# Revit family: ACORN_Flood_VIZULO
name_source: partatom
category: Lighting Fixtures
units: mm (PartAtom-declared; Revit-internal decimal feet)

## family parameters
Always vertical = Yes
Cut with Voids When Loaded = No
Light Source = Yes
OmniClass Number = 23.80.70.00
OmniClass Title = Lighting
Part Type = Normal
Room Calculation Point = No
Round Connector Dimension = Use Diameter
Shared = No
Work Plane-Based = No

## types (738) — shared parameters
Color Filter = 16777215
Dimming Lamp Color Temperature Shift = <None>
Emit Shape Visible in Rendering = No
Emit from Circle Diameter = 300 mm
Light Source Symbol Length = 3048 mm  [stored 10 ft]
Tilt Angle = 90.00°

## per-type parameters (varying)
| type | Default Elevation | Spot Beam Angle | Spot Field Angle |
| CO1, 20 W, 3000 K, 90° | 0 mm  [stored 0 ft] | 50.00° | 30.00° |
| CO1, 20 W, 4000 K, 90° | 0 mm  [stored 0 ft] | 30.00° | 50.00° |
| CO1, 270 W, 3000 K. 0° | 0 mm  [stored 0 ft] | 50.00° | 30.00° |
| CO1, 270 W, 4000 K, 0° | 0 mm  [stored 0 ft] | 50.00° | 30.00° |
| CO2, 20 W, 3000 K, 0° | 0 mm  [stored 0 ft] | 50.00° | 30.00° |
| CO2, 270 W, 4000 K, 0° | 0 mm  [stored 0 ft] | 50.00° | 30.00° |
| CO2, 20 W, 4000 K, 0° | 0 mm  [stored 0 ft] | 50.00° | 30.00° |
| CO2, 270 W, 3000 K, 0° | 0 mm  [stored 0 ft] | 50.00° | 30.00° |
| DO2, 20 W, 3000 K, 0° | 0 mm  [stored 0 ft] | 30.00° | 30.00° |
| DO2, 20 W, 4000 K, 0° | 0 mm  [stored 0 ft] | 30.00° | 30.00° |
| DO2, 270 W, 3000 K, 0° | 0 mm  [stored 0 ft] | 30.00° | 30.00° |
| DO2, 270 W, 4000 K, 0° | 0 mm  [stored 0 ft] | 30.00° | 30.00° |
| DO3, 20 W, 3000 K, 0° | 0 mm  [stored 0 ft] | 45.00° | 45.00° |
| DO3, 20 W, 4000 K, 0° | 0 mm  [stored 0 ft] | 45.00° | 45.00° |
| DO3, 270 W, 3000 K, 0° | 0 mm  [stored 0 ft] | 45.00° | 45.00° |
| DO3, 270 W, 4000 K, 0° | 0 mm  [stored 0 ft] | 45.00° | 45.00° |
| CO3, 20 W, 3000 K, 0° | 0 mm  [stored 0 ft] | 65.00° | 45.00° |
| CO3, 20 W, 4000 K, 0° | 0 mm  [stored 0 ft] | 65.00° | 45.00° |
| CO3, 270 W, 3000 K, 0° | 0 mm  [stored 0 ft] | 65.00° | 45.00° |
| CO3, 270 W, 4000 K, 0° | 0 mm  [stored 0 ft] | 65.00° | 45.00° |
| CO1, 20 W, 3000 K, 0° | 0 mm  [stored 0 ft] | 50.00° | 30.00° |
| CO1, 20 W, 3000 K, 180° | 0 mm  [stored 0 ft] | 50.00° | 30.00° |
| CO1, 20 W, 4000 K, 0° | 0 mm  [stored 0 ft] | 30.00° | 50.00° |
| CO1, 20 W, 4000 K, 180° | 0 mm  [stored 0 ft] | 30.00° | 50.00° |
| CO1, 270 W, 3000 K. 90° | 0 mm  [stored 0 ft] | 50.00° | 30.00° |
| CO1, 270 W, 3000 K. 180° | 0 mm  [stored 0 ft] | 50.00° | 30.00° |
| CO1, 270 W, 4000 K, 90° | 0 mm  [stored 0 ft] | 50.00° | 30.00° |
| CO1, 270 W, 4000 K, 180° | 0 mm  [stored 0 ft] | 50.00° | 30.00° |
| CO2, 20 W, 3000 K, 90° | 0 mm  [stored 0 ft] | 50.00° | 30.00° |
| CO2, 20 W, 3000 K, 180° | 0 mm  [stored 0 ft] | 50.00° | 30.00° |
| CO2, 20 W, 4000 K, 90° | 0 mm  [stored 0 ft] | 50.00° | 30.00° |
| CO2, 20 W, 4000 K, 180° | 0 mm  [stored 0 ft] | 50.00° | 30.00° |
| CO2, 270 W, 3000 K, 90° | 0 mm  [stored 0 ft] | 50.00° | 30.00° |
| CO2, 270 W, 3000 K, 180° | 0 mm  [stored 0 ft] | 50.00° | 30.00° |
| CO2, 270 W, 4000 K, 90° | 0 mm  [stored 0 ft] | 50.00° | 30.00° |
| CO2, 270 W, 4000 K, 180° | 0 mm  [stored 0 ft] | 50.00° | 30.00° |
| CO3, 20 W, 3000 K, 90° | 0 mm  [stored 0 ft] | 65.00° | 45.00° |
| CO3, 20 W, 3000 K, 180° | 0 mm  [stored 0 ft] | 65.00° | 45.00° |
| CO3, 20 W, 4000 K, 90° | 0 mm  [stored 0 ft] | 65.00° | 45.00° |
| CO3, 20 W, 4000 K, 180° | 0 mm  [stored 0 ft] | 65.00° | 45.00° |
| CO3, 270 W, 3000 K, 90° | 0 mm  [stored 0 ft] | 65.00° | 45.00° |
| CO3, 270 W, 3000 K, 180° | 0 mm  [stored 0 ft] | 65.00° | 45.00° |
| CO3, 270 W, 4000 K, 90° | 0 mm  [stored 0 ft] | 65.00° | 45.00° |
| CO3, 270 W, 4000 K, 180° | 0 mm  [stored 0 ft] | 65.00° | 45.00° |
| DO2, 20 W, 3000 K, 90° | 0 mm  [stored 0 ft] | 30.00° | 30.00° |
| DO2, 20 W, 3000 K, 180° | 0 mm  [stored 0 ft] | 30.00° | 30.00° |
| DO2, 20 W, 4000 K, 90° | 0 mm  [stored 0 ft] | 30.00° | 30.00° |
| DO2, 20 W, 4000 K, 180° | 0 mm  [stored 0 ft] | 30.00° | 30.00° |
| DO2, 270 W, 3000 K, 90° | 0 mm  [stored 0 ft] | 30.00° | 30.00° |
| DO2, 270 W, 3000 K, 180° | 0 mm  [stored 0 ft] | 30.00° | 30.00° |
| DO2, 270 W, 4000 K, 90° | 0 mm  [stored 0 ft] | 30.00° | 30.00° |
| DO2, 270 W, 4000 K, 180° | 0 mm  [stored 0 ft] | 30.00° | 30.00° |
| DO3, 20 W, 3000 K, 90° | 0 mm  [stored 0 ft] | 45.00° | 45.00° |
| DO3, 20 W, 3000 K, 180° | 0 mm  [stored 0 ft] | 45.00° | 45.00° |
| DO3, 20 W, 4000 K, 90° | 0 mm  [stored 0 ft] | 45.00° | 45.00° |
| DO3, 20 W, 4000 K, 180° | 0 mm  [stored 0 ft] | 45.00° | 45.00° |
| DO3, 270 W, 3000 K, 90° | 0 mm  [stored 0 ft] | 45.00° | 45.00° |
| DO3, 270 W, 3000 K, 180° | 0 mm  [stored 0 ft] | 45.00° | 45.00° |
| DO3, 270 W, 4000 K, 90° | 0 mm  [stored 0 ft] | 45.00° | 45.00° |
| DO3, 270 W, 4000 K, 180° | 0 mm  [stored 0 ft] | 45.00° | 45.00° |
| CO1, 20 W, 3000 K, 5° | 0 mm  [stored 0 ft] | 50.00° | 30.00° |
| CO1, 20 W, 3000 K, 10° | 0 mm  [stored 0 ft] | 50.00° | 30.00° |
| CO1, 20 W, 3000 K, 15° | 0 mm  [stored 0 ft] | 50.00° | 30.00° |
| CO1, 20 W, 3000 K, 20° | 0 mm  [stored 0 ft] | 50.00° | 30.00° |
| CO1, 20 W, 3000 K, 25° | 0 mm  [stored 0 ft] | 50.00° | 30.00° |
| CO1, 20 W, 3000 K, 30° | 0 mm  [stored 0 ft] | 50.00° | 30.00° |
| CO1, 20 W, 3000 K, 35° | 0 mm  [stored 0 ft] | 50.00° | 30.00° |
| CO1, 20 W, 3000 K, 40° | 0 mm  [stored 0 ft] | 50.00° | 30.00° |
| CO1, 20 W, 3000 K, 45° | 0 mm  [stored 0 ft] | 50.00° | 30.00° |
| CO1, 20 W, 3000 K, 50° | 0 mm  [stored 0 ft] | 50.00° | 30.00° |
| CO1, 20 W, 3000 K, 55° | 0 mm  [stored 0 ft] | 50.00° | 30.00° |
| CO1, 20 W, 3000 K, 60° | 0 mm  [stored 0 ft] | 50.00° | 30.00° |
| CO1, 20 W, 3000 K, 65° | 0 mm  [stored 0 ft] | 50.00° | 30.00° |
| CO1, 20 W, 3000 K, 70° | 0 mm  [stored 0 ft] | 50.00° | 30.00° |
| CO1, 20 W, 3000 K, 75° | 0 mm  [stored 0 ft] | 50.00° | 30.00° |
| CO1, 20 W, 3000 K, 80° | 0 mm  [stored 0 ft] | 50.00° | 30.00° |
| CO1, 20 W, 3000 K, 85° | 0 mm  [stored 0 ft] | 50.00° | 30.00° |
| CO1, 20 W, 3000 K, 95° | 0 mm  [stored 0 ft] | 50.00° | 30.00° |
| CO1, 20 W, 3000 K, 100° | 0 mm  [stored 0 ft] | 50.00° | 30.00° |
| CO1, 20 W, 3000 K, 105° | 0 mm  [stored 0 ft] | 50.00° | 30.00° |
| CO1, 20 W, 3000 K, 110° | 0 mm  [stored 0 ft] | 50.00° | 30.00° |
| CO1, 20 W, 3000 K, 115° | 0 mm  [stored 0 ft] | 50.00° | 30.00° |
| CO1, 20 W, 3000 K, 120° | 0 mm  [stored 0 ft] | 50.00° | 30.00° |
| CO1, 20 W, 3000 K, 125° | 0 mm  [stored 0 ft] | 50.00° | 30.00° |
| CO1, 20 W, 3000 K, 130° | 0 mm  [stored 0 ft] | 50.00° | 30.00° |
| CO1, 20 W, 3000 K, 135° | 0 mm  [stored 0 ft] | 50.00° | 30.00° |
| CO1, 20 W, 3000 K, 140° | 0 mm  [stored 0 ft] | 50.00° | 30.00° |
| CO1, 20 W, 3000 K, 145° | 0 mm  [stored 0 ft] | 50.00° | 30.00° |
| CO1, 20 W, 3000 K, 150° | 0 mm  [stored 0 ft] | 50.00° | 30.00° |
| CO1, 20 W, 3000 K, 165° | 0 mm  [stored 0 ft] | 50.00° | 30.00° |
| CO1, 20 W, 3000 K, 170° | 0 mm  [stored 0 ft] | 50.00° | 30.00° |
| CO1, 20 W, 3000 K, 175° | 0 mm  [stored 0 ft] | 50.00° | 30.00° |
| CO1, 20 W, 4000 K, 5° | 0 mm  [stored 0 ft] | 30.00° | 50.00° |
| CO1, 20 W, 4000 K, 10° | 0 mm  [stored 0 ft] | 30.00° | 50.00° |
| CO1, 20 W, 4000 K, 15° | 0 mm  [stored 0 ft] | 30.00° | 50.00° |
| CO1, 20 W, 4000 K, 20° | 0 mm  [stored 0 ft] | 30.00° | 50.00° |
| CO1, 20 W, 4000 K, 25° | 0 mm  [stored 0 ft] | 30.00° | 50.00° |
| CO1, 20 W, 4000 K, 30° | 0 mm  [stored 0 ft] | 30.00° | 50.00° |
| CO1, 20 W, 4000 K, 35° | 0 mm  [stored 0 ft] | 30.00° | 50.00° |
| CO1, 20 W, 4000 K, 40° | 0 mm  [stored 0 ft] | 30.00° | 50.00° |
| CO1, 20 W, 4000 K, 45° | 0 mm  [stored 0 ft] | 30.00° | 50.00° |
| CO1, 20 W, 4000 K, 50° | 0 mm  [stored 0 ft] | 30.00° | 50.00° |
| CO1, 20 W, 4000 K, 55° | 0 mm  [stored 0 ft] | 30.00° | 50.00° |
| CO1, 20 W, 4000 K, 60° | 0 mm  [stored 0 ft] | 30.00° | 50.00° |
| CO1, 20 W, 4000 K, 65° | 0 mm  [stored 0 ft] | 30.00° | 50.00° |
| CO1, 20 W, 4000 K, 70° | 0 mm  [stored 0 ft] | 30.00° | 50.00° |
| CO1, 20 W, 4000 K, 75° | 0 mm  [stored 0 ft] | 30.00° | 50.00° |
| CO1, 20 W, 4000 K, 80° | 0 mm  [stored 0 ft] | 30.00° | 50.00° |
| CO1, 20 W, 4000 K, 85° | 0 mm  [stored 0 ft] | 30.00° | 50.00° |
| CO1, 20 W, 4000 K, 95° | 0 mm  [stored 0 ft] | 30.00° | 50.00° |
| CO1, 20 W, 4000 K, 100° | 0 mm  [stored 0 ft] | 30.00° | 50.00° |
| CO1, 20 W, 4000 K, 105° | 0 mm  [stored 0 ft] | 30.00° | 50.00° |
| CO1, 20 W, 4000 K, 110° | 0 mm  [stored 0 ft] | 30.00° | 50.00° |
| CO1, 20 W, 4000 K, 115° | 0 mm  [stored 0 ft] | 30.00° | 50.00° |
| CO1, 20 W, 4000 K, 120° | 0 mm  [stored 0 ft] | 30.00° | 50.00° |
| CO1, 20 W, 4000 K, 125° | 0 mm  [stored 0 ft] | 30.00° | 50.00° |
| CO1, 20 W, 4000 K, 130° | 0 mm  [stored 0 ft] | 30.00° | 50.00° |
| CO1, 20 W, 4000 K, 135° | 0 mm  [stored 0 ft] | 30.00° | 50.00° |
| CO1, 20 W, 4000 K, 140° | 0 mm  [stored 0 ft] | 30.00° | 50.00° |
| CO1, 20 W, 4000 K, 145° | 0 mm  [stored 0 ft] | 30.00° | 50.00° |
| CO1, 20 W, 4000 K, 150° | 0 mm  [stored 0 ft] | 30.00° | 50.00° |
| CO1, 20 W, 4000 K, 155° | 0 mm  [stored 0 ft] | 30.00° | 50.00° |
| CO1, 20 W, 4000 K, 160° | 0 mm  [stored 0 ft] | 30.00° | 50.00° |
| CO1, 20 W, 4000 K, 165° | 0 mm  [stored 0 ft] | 30.00° | 50.00° |
| CO1, 20 W, 4000 K, 170° | 0 mm  [stored 0 ft] | 30.00° | 50.00° |
| CO1, 20 W, 4000 K, 175° | 0 mm  [stored 0 ft] | 30.00° | 50.00° |
| CO1, 270 W, 3000 K. 5° | 0 mm  [stored 0 ft] | 50.00° | 30.00° |
| CO1, 270 W, 3000 K. 10° | 0 mm  [stored 0 ft] | 50.00° | 30.00° |
| CO1, 270 W, 3000 K. 15° | 0 mm  [stored 0 ft] | 50.00° | 30.00° |
| CO1, 270 W, 3000 K. 20° | 0 mm  [stored 0 ft] | 50.00° | 30.00° |
| CO1, 270 W, 3000 K. 25° | 0 mm  [stored 0 ft] | 50.00° | 30.00° |
| CO1, 270 W, 3000 K. 30° | 0 mm  [stored 0 ft] | 50.00° | 30.00° |
| CO1, 270 W, 3000 K. 35° | 0 mm  [stored 0 ft] | 50.00° | 30.00° |
| CO1, 270 W, 3000 K. 40° | 0 mm  [stored 0 ft] | 50.00° | 30.00° |
| CO1, 270 W, 3000 K. 45° | 0 mm  [stored 0 ft] | 50.00° | 30.00° |
| CO1, 270 W, 3000 K. 50° | 0 mm  [stored 0 ft] | 50.00° | 30.00° |
| CO1, 270 W, 3000 K. 55° | 0 mm  [stored 0 ft] | 50.00° | 30.00° |
| CO1, 270 W, 3000 K. 60° | 0 mm  [stored 0 ft] | 50.00° | 30.00° |
| CO1, 270 W, 3000 K. 65° | 0 mm  [stored 0 ft] | 50.00° | 30.00° |
| CO1, 270 W, 3000 K. 70° | 0 mm  [stored 0 ft] | 50.00° | 30.00° |
| CO1, 270 W, 3000 K. 75° | 0 mm  [stored 0 ft] | 50.00° | 30.00° |
| CO1, 270 W, 3000 K. 80° | 0 mm  [stored 0 ft] | 50.00° | 30.00° |
| CO1, 270 W, 3000 K. 85° | 0 mm  [stored 0 ft] | 50.00° | 30.00° |
| CO1, 270 W, 3000 K. 95° | 0 mm  [stored 0 ft] | 50.00° | 30.00° |
| CO1, 270 W, 3000 K. 100° | 0 mm  [stored 0 ft] | 50.00° | 30.00° |
| CO1, 270 W, 3000 K. 105° | 0 mm  [stored 0 ft] | 50.00° | 30.00° |
| CO1, 270 W, 3000 K. 110° | 0 mm  [stored 0 ft] | 50.00° | 30.00° |
| CO1, 270 W, 3000 K. 115° | 0 mm  [stored 0 ft] | 50.00° | 30.00° |
| CO1, 270 W, 3000 K. 120° | 0 mm  [stored 0 ft] | 50.00° | 30.00° |
| CO1, 270 W, 3000 K. 125° | 0 mm  [stored 0 ft] | 50.00° | 30.00° |
| CO1, 270 W, 3000 K. 130° | 0 mm  [stored 0 ft] | 50.00° | 30.00° |
| CO1, 270 W, 3000 K. 135° | 0 mm  [stored 0 ft] | 50.00° | 30.00° |
| CO1, 270 W, 3000 K. 140° | 0 mm  [stored 0 ft] | 50.00° | 30.00° |
| CO1, 270 W, 3000 K. 145° | 0 mm  [stored 0 ft] | 50.00° | 30.00° |
| CO1, 270 W, 3000 K. 150° | 0 mm  [stored 0 ft] | 50.00° | 30.00° |
| CO1, 270 W, 3000 K. 155° | 0 mm  [stored 0 ft] | 50.00° | 30.00° |
| CO1, 270 W, 3000 K. 160° | 0 mm  [stored 0 ft] | 50.00° | 30.00° |
| CO1, 270 W, 3000 K. 165° | 0 mm  [stored 0 ft] | 50.00° | 30.00° |
| CO1, 270 W, 3000 K. 170° | 0 mm  [stored 0 ft] | 50.00° | 30.00° |
| CO1, 270 W, 3000 K. 175° | 0 mm  [stored 0 ft] | 50.00° | 30.00° |
| CO1, 270 W, 4000 K, 5° | 0 mm  [stored 0 ft] | 50.00° | 30.00° |
| CO1, 270 W, 4000 K, 10° | 0 mm  [stored 0 ft] | 50.00° | 30.00° |
| CO1, 270 W, 4000 K, 15° | 0 mm  [stored 0 ft] | 50.00° | 30.00° |
| CO1, 270 W, 4000 K, 20° | 0 mm  [stored 0 ft] | 50.00° | 30.00° |
| CO1, 270 W, 4000 K, 25° | 0 mm  [stored 0 ft] | 50.00° | 30.00° |
| CO1, 270 W, 4000 K, 30° | 0 mm  [stored 0 ft] | 50.00° | 30.00° |
| CO1, 270 W, 4000 K, 35° | 0 mm  [stored 0 ft] | 50.00° | 30.00° |
| CO1, 270 W, 4000 K, 40° | 0 mm  [stored 0 ft] | 50.00° | 30.00° |
| CO1, 270 W, 4000 K, 45° | 0 mm  [stored 0 ft] | 50.00° | 30.00° |
| CO1, 270 W, 4000 K, 50° | 0 mm  [stored 0 ft] | 50.00° | 30.00° |
| CO1, 270 W, 4000 K, 55° | 0 mm  [stored 0 ft] | 50.00° | 30.00° |
| CO1, 270 W, 4000 K, 60° | 0 mm  [stored 0 ft] | 50.00° | 30.00° |
| CO1, 270 W, 4000 K, 65° | 0 mm  [stored 0 ft] | 50.00° | 30.00° |
| CO1, 270 W, 4000 K, 70° | 0 mm  [stored 0 ft] | 50.00° | 30.00° |
| CO1, 270 W, 4000 K, 75° | 0 mm  [stored 0 ft] | 50.00° | 30.00° |
| CO1, 270 W, 4000 K, 80° | 0 mm  [stored 0 ft] | 50.00° | 30.00° |
| CO1, 270 W, 4000 K, 85° | 0 mm  [stored 0 ft] | 50.00° | 30.00° |
| CO1, 270 W, 4000 K, 95° | 0 mm  [stored 0 ft] | 50.00° | 30.00° |
| CO1, 270 W, 4000 K, 100° | 0 mm  [stored 0 ft] | 50.00° | 30.00° |
| CO1, 270 W, 4000 K, 105° | 0 mm  [stored 0 ft] | 50.00° | 30.00° |
| CO1, 270 W, 4000 K, 110° | 0 mm  [stored 0 ft] | 50.00° | 30.00° |
| CO1, 270 W, 4000 K, 115° | 0 mm  [stored 0 ft] | 50.00° | 30.00° |
| CO1, 270 W, 4000 K, 120° | 0 mm  [stored 0 ft] | 50.00° | 30.00° |
| CO1, 270 W, 4000 K, 125° | 0 mm  [stored 0 ft] | 50.00° | 30.00° |
| CO1, 270 W, 4000 K, 130° | 0 mm  [stored 0 ft] | 50.00° | 30.00° |
| CO1, 270 W, 4000 K, 135° | 0 mm  [stored 0 ft] | 50.00° | 30.00° |
| CO1, 270 W, 4000 K, 140° | 0 mm  [stored 0 ft] | 50.00° | 30.00° |
| CO1, 270 W, 4000 K, 145° | 0 mm  [stored 0 ft] | 50.00° | 30.00° |
| CO1, 270 W, 4000 K, 150° | 0 mm  [stored 0 ft] | 50.00° | 30.00° |
| CO1, 270 W, 4000 K, 155° | 0 mm  [stored 0 ft] | 50.00° | 30.00° |
| CO1, 270 W, 4000 K, 160° | 0 mm  [stored 0 ft] | 50.00° | 30.00° |
| CO1, 270 W, 4000 K, 165° | 0 mm  [stored 0 ft] | 50.00° | 30.00° |
| CO1, 270 W, 4000 K, 170° | 0 mm  [stored 0 ft] | 50.00° | 30.00° |
| CO1, 270 W, 4000 K, 175° | 0 mm  [stored 0 ft] | 50.00° | 30.00° |
| CO2, 20 W, 3000 K, 5° | 0 mm  [stored 0 ft] | 50.00° | 30.00° |
| CO2, 20 W, 3000 K, 10° | 0 mm  [stored 0 ft] | 50.00° | 30.00° |
| CO2, 20 W, 3000 K, 15° | 0 mm  [stored 0 ft] | 50.00° | 30.00° |
| CO2, 20 W, 3000 K, 20° | 0 mm  [stored 0 ft] | 50.00° | 30.00° |
| CO2, 20 W, 3000 K, 25° | 0 mm  [stored 0 ft] | 50.00° | 30.00° |
| CO2, 20 W, 3000 K, 30° | 0 mm  [stored 0 ft] | 50.00° | 30.00° |
| CO2, 20 W, 3000 K, 35° | 0 mm  [stored 0 ft] | 50.00° | 30.00° |
| CO2, 20 W, 3000 K, 40° | 0 mm  [stored 0 ft] | 50.00° | 30.00° |
| CO2, 20 W, 3000 K, 45° | 0 mm  [stored 0 ft] | 50.00° | 30.00° |
| CO2, 20 W, 3000 K, 50° | 0 mm  [stored 0 ft] | 50.00° | 30.00° |
| CO2, 20 W, 3000 K, 55° | 0 mm  [stored 0 ft] | 50.00° | 30.00° |
| CO2, 20 W, 3000 K, 60° | 0 mm  [stored 0 ft] | 50.00° | 30.00° |
| CO2, 20 W, 3000 K, 65° | 0 mm  [stored 0 ft] | 50.00° | 30.00° |
| CO2, 20 W, 3000 K, 70° | 0 mm  [stored 0 ft] | 50.00° | 30.00° |
| CO2, 20 W, 3000 K, 75° | 0 mm  [stored 0 ft] | 50.00° | 30.00° |
| CO2, 20 W, 3000 K, 80° | 0 mm  [stored 0 ft] | 50.00° | 30.00° |
| CO2, 20 W, 3000 K, 85° | 0 mm  [stored 0 ft] | 50.00° | 30.00° |
| CO2, 20 W, 3000 K, 95° | 0 mm  [stored 0 ft] | 50.00° | 30.00° |
| CO2, 20 W, 3000 K, 100° | 0 mm  [stored 0 ft] | 50.00° | 30.00° |
| CO2, 20 W, 3000 K, 105° | 0 mm  [stored 0 ft] | 50.00° | 30.00° |
| CO2, 20 W, 3000 K, 110° | 0 mm  [stored 0 ft] | 50.00° | 30.00° |
| CO2, 20 W, 3000 K, 115° | 0 mm  [stored 0 ft] | 50.00° | 30.00° |
| CO2, 20 W, 3000 K, 120° | 0 mm  [stored 0 ft] | 50.00° | 30.00° |
| CO2, 20 W, 3000 K, 125° | 0 mm  [stored 0 ft] | 50.00° | 30.00° |
| CO2, 20 W, 3000 K, 130° | 0 mm  [stored 0 ft] | 50.00° | 30.00° |
| CO2, 20 W, 3000 K, 135° | 0 mm  [stored 0 ft] | 50.00° | 30.00° |
| CO2, 20 W, 3000 K, 140° | 0 mm  [stored 0 ft] | 50.00° | 30.00° |
| CO2, 20 W, 3000 K, 145° | 0 mm  [stored 0 ft] | 50.00° | 30.00° |
| CO2, 20 W, 3000 K, 150° | 0 mm  [stored 0 ft] | 50.00° | 30.00° |
| CO2, 20 W, 3000 K, 155° | 0 mm  [stored 0 ft] | 50.00° | 30.00° |
| CO2, 20 W, 3000 K, 160° | 0 mm  [stored 0 ft] | 50.00° | 30.00° |
| CO2, 20 W, 3000 K, 165° | 0 mm  [stored 0 ft] | 50.00° | 30.00° |
| CO2, 20 W, 3000 K, 170° | 0 mm  [stored 0 ft] | 50.00° | 30.00° |
| CO2, 20 W, 3000 K, 175° | 0 mm  [stored 0 ft] | 50.00° | 30.00° |
| CO2, 20 W, 4000 K, 5° | 0 mm  [stored 0 ft] | 50.00° | 30.00° |
| CO2, 20 W, 4000 K, 10° | 0 mm  [stored 0 ft] | 50.00° | 30.00° |
| CO2, 20 W, 4000 K, 15° | 0 mm  [stored 0 ft] | 50.00° | 30.00° |
| CO2, 20 W, 4000 K, 20° | 0 mm  [stored 0 ft] | 50.00° | 30.00° |
| CO2, 20 W, 4000 K, 25° | 0 mm  [stored 0 ft] | 50.00° | 30.00° |
| CO2, 20 W, 4000 K, 30° | 0 mm  [stored 0 ft] | 50.00° | 30.00° |
| CO2, 20 W, 4000 K, 35° | 0 mm  [stored 0 ft] | 50.00° | 30.00° |
| CO2, 20 W, 4000 K, 40° | 0 mm  [stored 0 ft] | 50.00° | 30.00° |
| CO2, 20 W, 4000 K, 45° | 0 mm  [stored 0 ft] | 50.00° | 30.00° |
| CO2, 20 W, 4000 K, 50° | 0 mm  [stored 0 ft] | 50.00° | 30.00° |
| CO2, 20 W, 4000 K, 55° | 0 mm  [stored 0 ft] | 50.00° | 30.00° |
| CO2, 20 W, 4000 K, 60° | 0 mm  [stored 0 ft] | 50.00° | 30.00° |
| CO2, 20 W, 4000 K, 65° | 0 mm  [stored 0 ft] | 50.00° | 30.00° |
| CO2, 20 W, 4000 K, 70° | 0 mm  [stored 0 ft] | 50.00° | 30.00° |
| CO2, 20 W, 4000 K, 75° | 0 mm  [stored 0 ft] | 50.00° | 30.00° |
| CO2, 20 W, 4000 K, 80° | 0 mm  [stored 0 ft] | 50.00° | 30.00° |
| CO2, 20 W, 4000 K, 85° | 0 mm  [stored 0 ft] | 50.00° | 30.00° |
| CO2, 20 W, 4000 K, 95° | 0 mm  [stored 0 ft] | 50.00° | 30.00° |
| CO2, 20 W, 4000 K, 100° | 0 mm  [stored 0 ft] | 50.00° | 30.00° |
| CO2, 20 W, 4000 K, 105° | 0 mm  [stored 0 ft] | 50.00° | 30.00° |
| CO2, 20 W, 4000 K, 110° | 0 mm  [stored 0 ft] | 50.00° | 30.00° |
| CO2, 20 W, 4000 K, 115° | 0 mm  [stored 0 ft] | 50.00° | 30.00° |
| CO2, 20 W, 4000 K, 120° | 0 mm  [stored 0 ft] | 50.00° | 30.00° |
| CO2, 20 W, 4000 K, 125° | 0 mm  [stored 0 ft] | 50.00° | 30.00° |
| CO2, 20 W, 4000 K, 130° | 0 mm  [stored 0 ft] | 50.00° | 30.00° |
| CO2, 20 W, 4000 K, 135° | 0 mm  [stored 0 ft] | 50.00° | 30.00° |
| CO2, 20 W, 4000 K, 140° | 0 mm  [stored 0 ft] | 50.00° | 30.00° |
| CO2, 20 W, 4000 K, 145° | 0 mm  [stored 0 ft] | 50.00° | 30.00° |
| CO2, 20 W, 4000 K, 150° | 0 mm  [stored 0 ft] | 50.00° | 30.00° |
| CO2, 20 W, 4000 K, 155° | 0 mm  [stored 0 ft] | 50.00° | 30.00° |
| CO2, 20 W, 4000 K, 160° | 0 mm  [stored 0 ft] | 50.00° | 30.00° |
| CO2, 20 W, 4000 K, 165° | 0 mm  [stored 0 ft] | 50.00° | 30.00° |
| CO2, 20 W, 4000 K, 170° | 0 mm  [stored 0 ft] | 50.00° | 30.00° |
| CO2, 20 W, 4000 K, 175° | 0 mm  [stored 0 ft] | 50.00° | 30.00° |
| CO2, 270 W, 3000 K, 5° | 0 mm  [stored 0 ft] | 50.00° | 30.00° |
| CO2, 270 W, 3000 K, 10° | 0 mm  [stored 0 ft] | 50.00° | 30.00° |
| CO2, 270 W, 3000 K, 15° | 0 mm  [stored 0 ft] | 50.00° | 30.00° |
| CO2, 270 W, 3000 K, 20° | 0 mm  [stored 0 ft] | 50.00° | 30.00° |
| CO2, 270 W, 3000 K, 25° | 0 mm  [stored 0 ft] | 50.00° | 30.00° |
| CO2, 270 W, 3000 K, 30° | 0 mm  [stored 0 ft] | 50.00° | 30.00° |
| CO2, 270 W, 3000 K, 35° | 0 mm  [stored 0 ft] | 50.00° | 30.00° |
| CO2, 270 W, 3000 K, 40° | 0 mm  [stored 0 ft] | 50.00° | 30.00° |
| CO2, 270 W, 3000 K, 45° | 0 mm  [stored 0 ft] | 50.00° | 30.00° |
| CO2, 270 W, 3000 K, 50° | 0 mm  [stored 0 ft] | 50.00° | 30.00° |
| CO2, 270 W, 3000 K, 55° | 0 mm  [stored 0 ft] | 50.00° | 30.00° |
| CO2, 270 W, 3000 K, 60° | 0 mm  [stored 0 ft] | 50.00° | 30.00° |
| CO2, 270 W, 3000 K, 65° | 0 mm  [stored 0 ft] | 50.00° | 30.00° |
| CO2, 270 W, 3000 K, 70° | 0 mm  [stored 0 ft] | 50.00° | 30.00° |
| CO2, 270 W, 3000 K, 75° | 0 mm  [stored 0 ft] | 50.00° | 30.00° |
| CO2, 270 W, 3000 K, 80° | 0 mm  [stored 0 ft] | 50.00° | 30.00° |
| CO2, 270 W, 3000 K, 85° | 0 mm  [stored 0 ft] | 50.00° | 30.00° |
| CO2, 270 W, 3000 K, 95° | 0 mm  [stored 0 ft] | 50.00° | 30.00° |
| CO2, 270 W, 3000 K, 100° | 0 mm  [stored 0 ft] | 50.00° | 30.00° |
| CO2, 270 W, 3000 K, 105° | 0 mm  [stored 0 ft] | 50.00° | 30.00° |
| CO2, 270 W, 3000 K, 110° | 0 mm  [stored 0 ft] | 50.00° | 30.00° |
| CO2, 270 W, 3000 K, 115° | 0 mm  [stored 0 ft] | 50.00° | 30.00° |
| CO2, 270 W, 3000 K, 120° | 0 mm  [stored 0 ft] | 50.00° | 30.00° |
| CO2, 270 W, 3000 K, 125° | 0 mm  [stored 0 ft] | 50.00° | 30.00° |
| CO2, 270 W, 3000 K, 130° | 0 mm  [stored 0 ft] | 50.00° | 30.00° |
| CO2, 270 W, 3000 K, 135° | 0 mm  [stored 0 ft] | 50.00° | 30.00° |
| CO2, 270 W, 3000 K, 140° | 0 mm  [stored 0 ft] | 50.00° | 30.00° |
| CO2, 270 W, 3000 K, 145° | 0 mm  [stored 0 ft] | 50.00° | 30.00° |
| CO2, 270 W, 3000 K, 150° | 0 mm  [stored 0 ft] | 50.00° | 30.00° |
| CO2, 270 W, 3000 K, 155° | 0 mm  [stored 0 ft] | 50.00° | 30.00° |
| CO2, 270 W, 3000 K, 160° | 0 mm  [stored 0 ft] | 50.00° | 30.00° |
| CO2, 270 W, 3000 K, 165° | 0 mm  [stored 0 ft] | 50.00° | 30.00° |
| CO2, 270 W, 3000 K, 170° | 0 mm  [stored 0 ft] | 50.00° | 30.00° |
| CO2, 270 W, 3000 K, 175° | 0 mm  [stored 0 ft] | 50.00° | 30.00° |
| CO2, 270 W, 4000 K, 5° | 0 mm  [stored 0 ft] | 50.00° | 30.00° |
| CO2, 270 W, 4000 K, 10° | 0 mm  [stored 0 ft] | 50.00° | 30.00° |
| CO2, 270 W, 4000 K, 15° | 0 mm  [stored 0 ft] | 50.00° | 30.00° |
| CO2, 270 W, 4000 K, 20° | 0 mm  [stored 0 ft] | 50.00° | 30.00° |
| CO2, 270 W, 4000 K, 25° | 0 mm  [stored 0 ft] | 50.00° | 30.00° |
| CO2, 270 W, 4000 K, 30° | 0 mm  [stored 0 ft] | 50.00° | 30.00° |
| CO2, 270 W, 4000 K, 35° | 0 mm  [stored 0 ft] | 50.00° | 30.00° |
| CO2, 270 W, 4000 K, 40° | 0 mm  [stored 0 ft] | 50.00° | 30.00° |
| CO2, 270 W, 4000 K, 45° | 0 mm  [stored 0 ft] | 50.00° | 30.00° |
| CO2, 270 W, 4000 K, 50° | 0 mm  [stored 0 ft] | 50.00° | 30.00° |
| CO2, 270 W, 4000 K, 55° | 0 mm  [stored 0 ft] | 50.00° | 30.00° |
| CO2, 270 W, 4000 K, 60° | 0 mm  [stored 0 ft] | 50.00° | 30.00° |
| CO2, 270 W, 4000 K, 65° | 0 mm  [stored 0 ft] | 50.00° | 30.00° |
| CO2, 270 W, 4000 K, 70° | 0 mm  [stored 0 ft] | 50.00° | 30.00° |
| CO2, 270 W, 4000 K, 75° | 0 mm  [stored 0 ft] | 50.00° | 30.00° |
| CO2, 270 W, 4000 K, 80° | 0 mm  [stored 0 ft] | 50.00° | 30.00° |
| CO2, 270 W, 4000 K, 85° | 0 mm  [stored 0 ft] | 50.00° | 30.00° |
| CO2, 270 W, 4000 K, 95° | 0 mm  [stored 0 ft] | 50.00° | 30.00° |
| CO2, 270 W, 4000 K, 100° | 0 mm  [stored 0 ft] | 50.00° | 30.00° |
| CO2, 270 W, 4000 K, 105° | 0 mm  [stored 0 ft] | 50.00° | 30.00° |
| CO2, 270 W, 4000 K, 110° | 0 mm  [stored 0 ft] | 50.00° | 30.00° |
| CO2, 270 W, 4000 K, 115° | 0 mm  [stored 0 ft] | 50.00° | 30.00° |
| CO2, 270 W, 4000 K, 120° | 0 mm  [stored 0 ft] | 50.00° | 30.00° |
| CO2, 270 W, 4000 K, 125° | 0 mm  [stored 0 ft] | 50.00° | 30.00° |
| CO2, 270 W, 4000 K, 130° | 0 mm  [stored 0 ft] | 50.00° | 30.00° |
| CO2, 270 W, 4000 K, 135° | 0 mm  [stored 0 ft] | 50.00° | 30.00° |
| CO2, 270 W, 4000 K, 140° | 0 mm  [stored 0 ft] | 50.00° | 30.00° |
| CO2, 270 W, 4000 K, 145° | 0 mm  [stored 0 ft] | 50.00° | 30.00° |
| CO2, 270 W, 4000 K, 150° | 0 mm  [stored 0 ft] | 50.00° | 30.00° |
| CO2, 270 W, 4000 K, 155° | 0 mm  [stored 0 ft] | 50.00° | 30.00° |
| CO2, 270 W, 4000 K, 160° | 0 mm  [stored 0 ft] | 50.00° | 30.00° |
| CO2, 270 W, 4000 K, 165° | 0 mm  [stored 0 ft] | 50.00° | 30.00° |
| CO2, 270 W, 4000 K, 170° | 0 mm  [stored 0 ft] | 50.00° | 30.00° |
| CO2, 270 W, 4000 K, 175° | 0 mm  [stored 0 ft] | 50.00° | 30.00° |
| CO3, 20 W, 3000 K, 5° | 0 mm  [stored 0 ft] | 65.00° | 45.00° |
| CO3, 20 W, 3000 K, 10° | 0 mm  [stored 0 ft] | 65.00° | 45.00° |
| CO3, 20 W, 3000 K, 15° | 0 mm  [stored 0 ft] | 65.00° | 45.00° |
| CO3, 20 W, 3000 K, 20° | 0 mm  [stored 0 ft] | 65.00° | 45.00° |
| CO3, 20 W, 3000 K, 25° | 0 mm  [stored 0 ft] | 65.00° | 45.00° |
| CO3, 20 W, 3000 K, 30° | 0 mm  [stored 0 ft] | 65.00° | 45.00° |
| CO3, 20 W, 3000 K, 35° | 0 mm  [stored 0 ft] | 65.00° | 45.00° |
| CO3, 20 W, 3000 K, 40° | 0 mm  [stored 0 ft] | 65.00° | 45.00° |
| CO3, 20 W, 3000 K, 45° | 0 mm  [stored 0 ft] | 65.00° | 45.00° |
| CO3, 20 W, 3000 K, 50° | 0 mm  [stored 0 ft] | 65.00° | 45.00° |
| CO3, 20 W, 3000 K, 55° | 0 mm  [stored 0 ft] | 65.00° | 45.00° |
| CO3, 20 W, 3000 K, 60° | 0 mm  [stored 0 ft] | 65.00° | 45.00° |
| CO3, 20 W, 3000 K, 65° | 0 mm  [stored 0 ft] | 65.00° | 45.00° |
| CO3, 20 W, 3000 K, 70° | 0 mm  [stored 0 ft] | 65.00° | 45.00° |
| CO3, 20 W, 3000 K, 75° | 0 mm  [stored 0 ft] | 65.00° | 45.00° |
| CO3, 20 W, 3000 K, 80° | 0 mm  [stored 0 ft] | 65.00° | 45.00° |
| CO3, 20 W, 3000 K, 85° | 0 mm  [stored 0 ft] | 65.00° | 45.00° |
| CO3, 20 W, 3000 K, 95° | 0 mm  [stored 0 ft] | 65.00° | 45.00° |
| CO3, 20 W, 3000 K, 100° | 0 mm  [stored 0 ft] | 65.00° | 45.00° |
| CO3, 20 W, 3000 K, 105° | 0 mm  [stored 0 ft] | 65.00° | 45.00° |
| CO3, 20 W, 3000 K, 110° | 0 mm  [stored 0 ft] | 65.00° | 45.00° |
| CO3, 20 W, 3000 K, 115° | 0 mm  [stored 0 ft] | 65.00° | 45.00° |
| CO3, 20 W, 3000 K, 120° | 0 mm  [stored 0 ft] | 65.00° | 45.00° |
| CO3, 20 W, 3000 K, 125° | 0 mm  [stored 0 ft] | 65.00° | 45.00° |
| CO3, 20 W, 3000 K, 130° | 0 mm  [stored 0 ft] | 65.00° | 45.00° |
| CO3, 20 W, 3000 K, 135° | 0 mm  [stored 0 ft] | 65.00° | 45.00° |
| CO3, 20 W, 3000 K, 140° | 0 mm  [stored 0 ft] | 65.00° | 45.00° |
| CO3, 20 W, 3000 K, 145° | 0 mm  [stored 0 ft] | 65.00° | 45.00° |
| CO3, 20 W, 3000 K, 150° | 0 mm  [stored 0 ft] | 65.00° | 45.00° |
| CO3, 20 W, 3000 K, 155° | 0 mm  [stored 0 ft] | 65.00° | 45.00° |
| CO3, 20 W, 3000 K, 160° | 0 mm  [stored 0 ft] | 65.00° | 45.00° |
| CO3, 20 W, 3000 K, 165° | 0 mm  [stored 0 ft] | 65.00° | 45.00° |
| CO3, 20 W, 3000 K, 170° | 0 mm  [stored 0 ft] | 65.00° | 45.00° |
| CO3, 20 W, 3000 K, 175° | 0 mm  [stored 0 ft] | 65.00° | 45.00° |
| CO3, 20 W, 4000 K, 5° | 0 mm  [stored 0 ft] | 65.00° | 45.00° |
| CO3, 20 W, 4000 K, 10° | 0 mm  [stored 0 ft] | 65.00° | 45.00° |
| CO3, 20 W, 4000 K, 15° | 0 mm  [stored 0 ft] | 65.00° | 45.00° |
| CO3, 20 W, 4000 K, 20° | 0 mm  [stored 0 ft] | 65.00° | 45.00° |
| CO3, 20 W, 4000 K, 25° | 0 mm  [stored 0 ft] | 65.00° | 45.00° |
| CO3, 20 W, 4000 K, 30° | 0 mm  [stored 0 ft] | 65.00° | 45.00° |
| CO3, 20 W, 4000 K, 35° | 0 mm  [stored 0 ft] | 65.00° | 45.00° |
| CO3, 20 W, 4000 K, 40° | 0 mm  [stored 0 ft] | 65.00° | 45.00° |
| CO3, 20 W, 4000 K, 45° | 0 mm  [stored 0 ft] | 65.00° | 45.00° |
| CO3, 20 W, 4000 K, 50° | 0 mm  [stored 0 ft] | 65.00° | 45.00° |
| CO3, 20 W, 4000 K, 55° | 0 mm  [stored 0 ft] | 65.00° | 45.00° |
| CO3, 20 W, 4000 K, 60° | 0 mm  [stored 0 ft] | 65.00° | 45.00° |
| CO3, 20 W, 4000 K, 65° | 0 mm  [stored 0 ft] | 65.00° | 45.00° |
| CO3, 20 W, 4000 K, 70° | 0 mm  [stored 0 ft] | 65.00° | 45.00° |
| CO3, 20 W, 4000 K, 75° | 0 mm  [stored 0 ft] | 65.00° | 45.00° |
| CO3, 20 W, 4000 K, 80° | 0 mm  [stored 0 ft] | 65.00° | 45.00° |
| CO3, 20 W, 4000 K, 85° | 0 mm  [stored 0 ft] | 65.00° | 45.00° |
| CO3, 20 W, 4000 K, 95° | 0 mm  [stored 0 ft] | 65.00° | 45.00° |
| CO3, 20 W, 4000 K, 100° | 0 mm  [stored 0 ft] | 65.00° | 45.00° |
| CO3, 20 W, 4000 K, 105° | 0 mm  [stored 0 ft] | 65.00° | 45.00° |
| CO3, 20 W, 4000 K, 110° | 0 mm  [stored 0 ft] | 65.00° | 45.00° |
| CO3, 20 W, 4000 K, 115° | 0 mm  [stored 0 ft] | 65.00° | 45.00° |
| CO3, 20 W, 4000 K, 120° | 0 mm  [stored 0 ft] | 65.00° | 45.00° |
| CO3, 20 W, 4000 K, 125° | 0 mm  [stored 0 ft] | 65.00° | 45.00° |
| CO3, 20 W, 4000 K, 130° | 0 mm  [stored 0 ft] | 65.00° | 45.00° |
| CO3, 20 W, 4000 K, 135° | 0 mm  [stored 0 ft] | 65.00° | 45.00° |
| CO3, 20 W, 4000 K, 140° | 0 mm  [stored 0 ft] | 65.00° | 45.00° |
| CO3, 20 W, 4000 K, 145° | 0 mm  [stored 0 ft] | 65.00° | 45.00° |
| CO3, 20 W, 4000 K, 150° | 0 mm  [stored 0 ft] | 65.00° | 45.00° |
| CO3, 20 W, 4000 K, 155° | 0 mm  [stored 0 ft] | 65.00° | 45.00° |
| CO3, 20 W, 4000 K, 160° | 0 mm  [stored 0 ft] | 65.00° | 45.00° |
| CO3, 20 W, 4000 K, 165° | 0 mm  [stored 0 ft] | 65.00° | 45.00° |
| CO3, 20 W, 4000 K, 170° | 0 mm  [stored 0 ft] | 65.00° | 45.00° |
| CO3, 20 W, 4000 K, 175° | 0 mm  [stored 0 ft] | 65.00° | 45.00° |
| CO3, 270 W, 3000 K, 5° | 0 mm  [stored 0 ft] | 65.00° | 45.00° |
| CO3, 270 W, 3000 K, 10° | 0 mm  [stored 0 ft] | 65.00° | 45.00° |
| CO3, 270 W, 3000 K, 15° | 0 mm  [stored 0 ft] | 65.00° | 45.00° |
| CO3, 270 W, 3000 K, 20° | 0 mm  [stored 0 ft] | 65.00° | 45.00° |
| CO3, 270 W, 3000 K, 25° | 0 mm  [stored 0 ft] | 65.00° | 45.00° |
| CO3, 270 W, 3000 K, 30° | 0 mm  [stored 0 ft] | 65.00° | 45.00° |
| CO3, 270 W, 3000 K, 35° | 0 mm  [stored 0 ft] | 65.00° | 45.00° |
| CO3, 270 W, 3000 K, 40° | 0 mm  [stored 0 ft] | 65.00° | 45.00° |
| CO3, 270 W, 3000 K, 45° | 0 mm  [stored 0 ft] | 65.00° | 45.00° |
| CO3, 270 W, 3000 K, 50° | 0 mm  [stored 0 ft] | 65.00° | 45.00° |
| CO3, 270 W, 3000 K, 55° | 0 mm  [stored 0 ft] | 65.00° | 45.00° |
| CO3, 270 W, 3000 K, 60° | 0 mm  [stored 0 ft] | 65.00° | 45.00° |
| CO3, 270 W, 3000 K, 65° | 0 mm  [stored 0 ft] | 65.00° | 45.00° |
| CO3, 270 W, 3000 K, 70° | 0 mm  [stored 0 ft] | 65.00° | 45.00° |
| CO3, 270 W, 3000 K, 75° | 0 mm  [stored 0 ft] | 65.00° | 45.00° |
| CO3, 270 W, 3000 K, 80° | 0 mm  [stored 0 ft] | 65.00° | 45.00° |
| CO3, 270 W, 3000 K, 85° | 0 mm  [stored 0 ft] | 65.00° | 45.00° |
| CO3, 270 W, 3000 K, 95° | 0 mm  [stored 0 ft] | 65.00° | 45.00° |
| CO3, 270 W, 3000 K, 100° | 0 mm  [stored 0 ft] | 65.00° | 45.00° |
| CO3, 270 W, 3000 K, 105° | 0 mm  [stored 0 ft] | 65.00° | 45.00° |
| CO3, 270 W, 3000 K, 110° | 0 mm  [stored 0 ft] | 65.00° | 45.00° |
| CO3, 270 W, 3000 K, 115° | 0 mm  [stored 0 ft] | 65.00° | 45.00° |
| CO3, 270 W, 3000 K, 120° | 0 mm  [stored 0 ft] | 65.00° | 45.00° |
| CO3, 270 W, 3000 K, 125° | 0 mm  [stored 0 ft] | 65.00° | 45.00° |
| CO3, 270 W, 3000 K, 130° | 0 mm  [stored 0 ft] | 65.00° | 45.00° |
| CO3, 270 W, 3000 K, 135° | 0 mm  [stored 0 ft] | 65.00° | 45.00° |
| CO3, 270 W, 3000 K, 140° | 0 mm  [stored 0 ft] | 65.00° | 45.00° |
| CO3, 270 W, 3000 K, 145° | 0 mm  [stored 0 ft] | 65.00° | 45.00° |
| CO3, 270 W, 3000 K, 150° | 0 mm  [stored 0 ft] | 65.00° | 45.00° |
| CO3, 270 W, 3000 K, 155° | 0 mm  [stored 0 ft] | 65.00° | 45.00° |
| CO3, 270 W, 3000 K, 160° | 0 mm  [stored 0 ft] | 65.00° | 45.00° |
| CO3, 270 W, 3000 K, 165° | 0 mm  [stored 0 ft] | 65.00° | 45.00° |
| CO3, 270 W, 3000 K, 170° | 0 mm  [stored 0 ft] | 65.00° | 45.00° |
| CO3, 270 W, 3000 K, 175° | 0 mm  [stored 0 ft] | 65.00° | 45.00° |
| CO3, 270 W, 4000 K, 5° | 0 mm  [stored 0 ft] | 65.00° | 45.00° |
| CO3, 270 W, 4000 K, 10° | 0 mm  [stored 0 ft] | 65.00° | 45.00° |
| CO3, 270 W, 4000 K, 15° | 0 mm  [stored 0 ft] | 65.00° | 45.00° |
| CO3, 270 W, 4000 K, 20° | 0 mm  [stored 0 ft] | 65.00° | 45.00° |
| CO3, 270 W, 4000 K, 25° | 0 mm  [stored 0 ft] | 65.00° | 45.00° |
| CO3, 270 W, 4000 K, 30° | 0 mm  [stored 0 ft] | 65.00° | 45.00° |
| CO3, 270 W, 4000 K, 35° | 0 mm  [stored 0 ft] | 65.00° | 45.00° |
| CO3, 270 W, 4000 K, 40° | 0 mm  [stored 0 ft] | 65.00° | 45.00° |
| CO3, 270 W, 4000 K, 45° | 0 mm  [stored 0 ft] | 65.00° | 45.00° |
| CO3, 270 W, 4000 K, 50° | 0 mm  [stored 0 ft] | 65.00° | 45.00° |
| CO3, 270 W, 4000 K, 55° | 0 mm  [stored 0 ft] | 65.00° | 45.00° |
| CO3, 270 W, 4000 K, 60° | 0 mm  [stored 0 ft] | 65.00° | 45.00° |
| CO3, 270 W, 4000 K, 65° | 0 mm  [stored 0 ft] | 65.00° | 45.00° |
| CO3, 270 W, 4000 K, 70° | 0 mm  [stored 0 ft] | 65.00° | 45.00° |
| CO3, 270 W, 4000 K, 75° | 0 mm  [stored 0 ft] | 65.00° | 45.00° |
| CO3, 270 W, 4000 K, 80° | 0 mm  [stored 0 ft] | 65.00° | 45.00° |
| CO3, 270 W, 4000 K, 85° | 0 mm  [stored 0 ft] | 65.00° | 45.00° |
| CO3, 270 W, 4000 K, 95° | 0 mm  [stored 0 ft] | 65.00° | 45.00° |
| CO3, 270 W, 4000 K, 100° | 0 mm  [stored 0 ft] | 65.00° | 45.00° |
| CO3, 270 W, 4000 K, 105° | 0 mm  [stored 0 ft] | 65.00° | 45.00° |
| CO3, 270 W, 4000 K, 110° | 1 mm  [stored 0.00328084 ft] | 65.00° | 45.00° |
| CO3, 270 W, 4000 K, 115° | 0 mm  [stored 0 ft] | 65.00° | 45.00° |
| CO3, 270 W, 4000 K, 120° | 0 mm  [stored 0 ft] | 65.00° | 45.00° |
| CO3, 270 W, 4000 K, 125° | 0 mm  [stored 0 ft] | 65.00° | 45.00° |
| CO3, 270 W, 4000 K, 130° | 0 mm  [stored 0 ft] | 65.00° | 45.00° |
| CO3, 270 W, 4000 K, 135° | 0 mm  [stored 0 ft] | 65.00° | 45.00° |
| CO3, 270 W, 4000 K, 140° | 0 mm  [stored 0 ft] | 65.00° | 45.00° |
| CO3, 270 W, 4000 K, 145° | 0 mm  [stored 0 ft] | 65.00° | 45.00° |
| CO3, 270 W, 4000 K, 150° | 0 mm  [stored 0 ft] | 65.00° | 45.00° |
| CO3, 270 W, 4000 K, 155° | 0 mm  [stored 0 ft] | 65.00° | 45.00° |
| CO3, 270 W, 4000 K, 160° | 0 mm  [stored 0 ft] | 65.00° | 45.00° |
| CO3, 270 W, 4000 K, 165° | 0 mm  [stored 0 ft] | 65.00° | 45.00° |
| CO3, 270 W, 4000 K, 170° | 0 mm  [stored 0 ft] | 65.00° | 45.00° |
| CO3, 270 W, 4000 K, 175° | 0 mm  [stored 0 ft] | 65.00° | 45.00° |
| DO2, 20 W, 3000 K, 5° | 0 mm  [stored 0 ft] | 30.00° | 30.00° |
| DO2, 20 W, 3000 K, 10° | 0 mm  [stored 0 ft] | 30.00° | 30.00° |
| DO2, 20 W, 3000 K, 15° | 0 mm  [stored 0 ft] | 30.00° | 30.00° |
| DO2, 20 W, 3000 K, 20° | 0 mm  [stored 0 ft] | 30.00° | 30.00° |
| DO2, 20 W, 3000 K, 25° | 0 mm  [stored 0 ft] | 30.00° | 30.00° |
| DO2, 20 W, 3000 K, 30° | 0 mm  [stored 0 ft] | 30.00° | 30.00° |
| DO2, 20 W, 3000 K, 35° | 0 mm  [stored 0 ft] | 30.00° | 30.00° |
| DO2, 20 W, 3000 K, 40° | 0 mm  [stored 0 ft] | 30.00° | 30.00° |
| DO2, 20 W, 3000 K, 45° | 0 mm  [stored 0 ft] | 30.00° | 30.00° |
| DO2, 20 W, 3000 K, 50° | 0 mm  [stored 0 ft] | 30.00° | 30.00° |
| DO2, 20 W, 3000 K, 55° | 0 mm  [stored 0 ft] | 30.00° | 30.00° |
| DO2, 20 W, 3000 K, 60° | 0 mm  [stored 0 ft] | 30.00° | 30.00° |
| DO2, 20 W, 3000 K, 65° | 0 mm  [stored 0 ft] | 30.00° | 30.00° |
| DO2, 20 W, 3000 K, 70° | 0 mm  [stored 0 ft] | 30.00° | 30.00° |
| DO2, 20 W, 3000 K, 75° | 0 mm  [stored 0 ft] | 30.00° | 30.00° |
| DO2, 20 W, 3000 K, 80° | 0 mm  [stored 0 ft] | 30.00° | 30.00° |
| DO2, 20 W, 3000 K, 85° | 0 mm  [stored 0 ft] | 30.00° | 30.00° |
| DO2, 20 W, 3000 K, 95° | 9 mm  [stored 0.0295276 ft] | 30.00° | 30.00° |
| DO2, 20 W, 3000 K, 105° | 0 mm  [stored 0 ft] | 30.00° | 30.00° |
| DO2, 20 W, 3000 K, 100° | 0 mm  [stored 0 ft] | 30.00° | 30.00° |
| DO2, 20 W, 3000 K, 110° | 0 mm  [stored 0 ft] | 30.00° | 30.00° |
| DO2, 20 W, 3000 K, 115° | 0 mm  [stored 0 ft] | 30.00° | 30.00° |
| DO2, 20 W, 3000 K, 120° | 0 mm  [stored 0 ft] | 30.00° | 30.00° |
| DO2, 20 W, 3000 K, 125° | 0 mm  [stored 0 ft] | 30.00° | 30.00° |
| DO2, 20 W, 3000 K, 130° | 0 mm  [stored 0 ft] | 30.00° | 30.00° |
| DO2, 20 W, 3000 K, 135° | 0 mm  [stored 0 ft] | 30.00° | 30.00° |
| DO2, 20 W, 3000 K, 140° | 0 mm  [stored 0 ft] | 30.00° | 30.00° |
| DO2, 20 W, 3000 K, 145° | 0 mm  [stored 0 ft] | 30.00° | 30.00° |
| DO2, 20 W, 3000 K, 150° | 0 mm  [stored 0 ft] | 30.00° | 30.00° |
| DO2, 20 W, 3000 K, 155° | 0 mm  [stored 0 ft] | 30.00° | 30.00° |
| DO2, 20 W, 3000 K, 160° | 0 mm  [stored 0 ft] | 30.00° | 30.00° |
| DO2, 20 W, 3000 K, 165° | 0 mm  [stored 0 ft] | 30.00° | 30.00° |
| DO2, 20 W, 3000 K, 170° | 0 mm  [stored 0 ft] | 30.00° | 30.00° |
| DO2, 20 W, 3000 K, 175° | 0 mm  [stored 0 ft] | 30.00° | 30.00° |
| DO2, 20 W, 4000 K, 5° | 0 mm  [stored 0 ft] | 30.00° | 30.00° |
| DO2, 20 W, 4000 K, 10° | 0 mm  [stored 0 ft] | 30.00° | 30.00° |
| DO2, 20 W, 4000 K, 15° | 0 mm  [stored 0 ft] | 30.00° | 30.00° |
| DO2, 20 W, 4000 K, 20° | 0 mm  [stored 0 ft] | 30.00° | 30.00° |
| DO2, 20 W, 4000 K, 25° | 0 mm  [stored 0 ft] | 30.00° | 30.00° |
| DO2, 20 W, 4000 K, 30° | 0 mm  [stored 0 ft] | 30.00° | 30.00° |
| DO2, 20 W, 4000 K, 35° | 0 mm  [stored 0 ft] | 30.00° | 30.00° |
| DO2, 20 W, 4000 K, 40° | 0 mm  [stored 0 ft] | 30.00° | 30.00° |
| DO2, 20 W, 4000 K, 45° | 0 mm  [stored 0 ft] | 30.00° | 30.00° |
| DO2, 20 W, 4000 K, 50° | 0 mm  [stored 0 ft] | 30.00° | 30.00° |
| DO2, 20 W, 4000 K, 55° | 0 mm  [stored 0 ft] | 30.00° | 30.00° |
| DO2, 20 W, 4000 K, 60° | 0 mm  [stored 0 ft] | 30.00° | 30.00° |
| DO2, 20 W, 4000 K, 65° | 0 mm  [stored 0 ft] | 30.00° | 30.00° |
| DO2, 20 W, 4000 K, 70° | 0 mm  [stored 0 ft] | 30.00° | 30.00° |
| DO2, 20 W, 4000 K, 75° | 0 mm  [stored 0 ft] | 30.00° | 30.00° |
| DO2, 20 W, 4000 K, 80° | 0 mm  [stored 0 ft] | 30.00° | 30.00° |
| DO2, 20 W, 4000 K, 85° | 0 mm  [stored 0 ft] | 30.00° | 30.00° |
| DO2, 20 W, 4000 K, 95° | 0 mm  [stored 0 ft] | 30.00° | 30.00° |
| DO2, 20 W, 4000 K, 100° | 0 mm  [stored 0 ft] | 30.00° | 30.00° |
| DO2, 20 W, 4000 K, 105° | 0 mm  [stored 0 ft] | 30.00° | 30.00° |
| DO2, 20 W, 4000 K, 110° | 0 mm  [stored 0 ft] | 30.00° | 30.00° |
| DO2, 20 W, 4000 K, 115° | 0 mm  [stored 0 ft] | 30.00° | 30.00° |
| DO2, 20 W, 4000 K, 120° | 0 mm  [stored 0 ft] | 30.00° | 30.00° |
| DO2, 20 W, 4000 K, 125° | 0 mm  [stored 0 ft] | 30.00° | 30.00° |
| DO2, 20 W, 4000 K, 130° | 0 mm  [stored 0 ft] | 30.00° | 30.00° |
| DO2, 20 W, 4000 K, 135° | 0 mm  [stored 0 ft] | 30.00° | 30.00° |
| DO2, 20 W, 4000 K, 140° | 0 mm  [stored 0 ft] | 30.00° | 30.00° |
| DO2, 20 W, 4000 K, 145° | 0 mm  [stored 0 ft] | 30.00° | 30.00° |
| DO2, 20 W, 4000 K, 150° | 0 mm  [stored 0 ft] | 30.00° | 30.00° |
| DO2, 20 W, 4000 K, 155° | 0 mm  [stored 0 ft] | 30.00° | 30.00° |
| DO2, 20 W, 4000 K, 160° | 0 mm  [stored 0 ft] | 30.00° | 30.00° |
| DO2, 20 W, 4000 K, 165° | 0 mm  [stored 0 ft] | 30.00° | 30.00° |
| DO2, 20 W, 4000 K, 170° | 0 mm  [stored 0 ft] | 30.00° | 30.00° |
| DO2, 20 W, 4000 K, 175° | 0 mm  [stored 0 ft] | 30.00° | 30.00° |
| DO2, 270 W, 3000 K, 5° | 0 mm  [stored 0 ft] | 30.00° | 30.00° |
| DO2, 270 W, 3000 K, 10° | 0 mm  [stored 0 ft] | 30.00° | 30.00° |
| DO2, 270 W, 3000 K, 15° | 0 mm  [stored 0 ft] | 30.00° | 30.00° |
| DO2, 270 W, 3000 K, 20° | 0 mm  [stored 0 ft] | 30.00° | 30.00° |
| DO2, 270 W, 3000 K, 25° | 0 mm  [stored 0 ft] | 30.00° | 30.00° |
| DO2, 270 W, 3000 K, 30° | 0 mm  [stored 0 ft] | 30.00° | 30.00° |
| DO2, 270 W, 3000 K, 35° | 0 mm  [stored 0 ft] | 30.00° | 30.00° |
| DO2, 270 W, 3000 K, 40° | 0 mm  [stored 0 ft] | 30.00° | 30.00° |
| DO2, 270 W, 3000 K, 45° | 0 mm  [stored 0 ft] | 30.00° | 30.00° |
| DO2, 270 W, 3000 K, 50° | 0 mm  [stored 0 ft] | 30.00° | 30.00° |
| DO2, 270 W, 3000 K, 55° | 0 mm  [stored 0 ft] | 30.00° | 30.00° |
| DO2, 270 W, 3000 K, 60° | 0 mm  [stored 0 ft] | 30.00° | 30.00° |
| DO2, 270 W, 3000 K, 65° | 0 mm  [stored 0 ft] | 30.00° | 30.00° |
| DO2, 270 W, 3000 K, 70° | 0 mm  [stored 0 ft] | 30.00° | 30.00° |
| DO2, 270 W, 3000 K, 75° | 0 mm  [stored 0 ft] | 30.00° | 30.00° |
| DO2, 270 W, 3000 K, 80° | 0 mm  [stored 0 ft] | 30.00° | 30.00° |
| DO2, 270 W, 3000 K, 85° | 0 mm  [stored 0 ft] | 30.00° | 30.00° |
| DO2, 270 W, 3000 K, 95° | 0 mm  [stored 0 ft] | 30.00° | 30.00° |
| DO2, 270 W, 3000 K, 100° | 0 mm  [stored 0 ft] | 30.00° | 30.00° |
| DO2, 270 W, 3000 K, 105° | 0 mm  [stored 0 ft] | 30.00° | 30.00° |
| DO2, 270 W, 3000 K, 110° | 0 mm  [stored 0 ft] | 30.00° | 30.00° |
| DO2, 270 W, 3000 K, 115° | 0 mm  [stored 0 ft] | 30.00° | 30.00° |
| DO2, 270 W, 3000 K, 120° | 0 mm  [stored 0 ft] | 30.00° | 30.00° |
| DO2, 270 W, 3000 K, 125° | 0 mm  [stored 0 ft] | 30.00° | 30.00° |
| DO2, 270 W, 3000 K, 130° | 0 mm  [stored 0 ft] | 30.00° | 30.00° |
| DO2, 270 W, 3000 K, 135° | 0 mm  [stored 0 ft] | 30.00° | 30.00° |
| DO2, 270 W, 3000 K, 140° | 0 mm  [stored 0 ft] | 30.00° | 30.00° |
| DO2, 270 W, 3000 K, 145° | 0 mm  [stored 0 ft] | 30.00° | 30.00° |
| DO2, 270 W, 3000 K, 150° | 0 mm  [stored 0 ft] | 30.00° | 30.00° |
| DO2, 270 W, 3000 K, 155° | 0 mm  [stored 0 ft] | 30.00° | 30.00° |
| DO2, 270 W, 3000 K, 160° | 0 mm  [stored 0 ft] | 30.00° | 30.00° |
| DO2, 270 W, 3000 K, 165° | 0 mm  [stored 0 ft] | 30.00° | 30.00° |
| DO2, 270 W, 3000 K, 170° | 0 mm  [stored 0 ft] | 30.00° | 30.00° |
| DO2, 270 W, 3000 K, 175° | 0 mm  [stored 0 ft] | 30.00° | 30.00° |
| DO2, 270 W, 4000 K, 5° | 0 mm  [stored 0 ft] | 30.00° | 30.00° |
| DO2, 270 W, 4000 K, 10° | 0 mm  [stored 0 ft] | 30.00° | 30.00° |
| DO2, 270 W, 4000 K, 15° | 0 mm  [stored 0 ft] | 30.00° | 30.00° |
| DO2, 270 W, 4000 K, 20° | 0 mm  [stored 0 ft] | 30.00° | 30.00° |
| DO2, 270 W, 4000 K, 25° | 0 mm  [stored 0 ft] | 30.00° | 30.00° |
| DO2, 270 W, 4000 K, 30° | 0 mm  [stored 0 ft] | 30.00° | 30.00° |
| DO2, 270 W, 4000 K, 35° | 0 mm  [stored 0 ft] | 30.00° | 30.00° |
| DO2, 270 W, 4000 K, 40° | 0 mm  [stored 0 ft] | 30.00° | 30.00° |
| DO2, 270 W, 4000 K, 45° | 0 mm  [stored 0 ft] | 30.00° | 30.00° |
| DO2, 270 W, 4000 K, 50° | 0 mm  [stored 0 ft] | 30.00° | 30.00° |
| DO2, 270 W, 4000 K, 55° | 0 mm  [stored 0 ft] | 30.00° | 30.00° |
| DO2, 270 W, 4000 K, 60° | 0 mm  [stored 0 ft] | 30.00° | 30.00° |
| DO2, 270 W, 4000 K, 65° | 0 mm  [stored 0 ft] | 30.00° | 30.00° |
| DO2, 270 W, 4000 K, 70° | 0 mm  [stored 0 ft] | 30.00° | 30.00° |
| DO2, 270 W, 4000 K, 75° | 0 mm  [stored 0 ft] | 30.00° | 30.00° |
| DO2, 270 W, 4000 K, 80° | 0 mm  [stored 0 ft] | 30.00° | 30.00° |
| DO2, 270 W, 4000 K, 85° | 8 mm  [stored 0.0262467 ft] | 30.00° | 30.00° |
| DO2, 270 W, 4000 K, 95° | 0 mm  [stored 0 ft] | 30.00° | 30.00° |
| DO2, 270 W, 4000 K, 100° | 0 mm  [stored 0 ft] | 30.00° | 30.00° |
| DO2, 270 W, 4000 K, 105° | 0 mm  [stored 0 ft] | 30.00° | 30.00° |
| DO2, 270 W, 4000 K, 110° | 0 mm  [stored 0 ft] | 30.00° | 30.00° |
| DO2, 270 W, 4000 K, 115° | 0 mm  [stored 0 ft] | 30.00° | 30.00° |
| DO2, 270 W, 4000 K, 120° | 0 mm  [stored 0 ft] | 30.00° | 30.00° |
| DO2, 270 W, 4000 K, 125° | 0 mm  [stored 0 ft] | 30.00° | 30.00° |
| DO2, 270 W, 4000 K, 130° | 0 mm  [stored 0 ft] | 30.00° | 30.00° |
| DO2, 270 W, 4000 K, 135° | 0 mm  [stored 0 ft] | 30.00° | 30.00° |
| DO2, 270 W, 4000 K, 140° | 0 mm  [stored 0 ft] | 30.00° | 30.00° |
| DO2, 270 W, 4000 K, 145° | 0 mm  [stored 0 ft] | 30.00° | 30.00° |
| DO2, 270 W, 4000 K, 150° | 0 mm  [stored 0 ft] | 30.00° | 30.00° |
| DO2, 270 W, 4000 K, 155° | 0 mm  [stored 0 ft] | 30.00° | 30.00° |
| DO2, 270 W, 4000 K, 160° | 0 mm  [stored 0 ft] | 30.00° | 30.00° |
| DO2, 270 W, 4000 K, 165° | 0 mm  [stored 0 ft] | 30.00° | 30.00° |
| DO2, 270 W, 4000 K, 170° | 0 mm  [stored 0 ft] | 30.00° | 30.00° |
| DO2, 270 W, 4000 K, 175° | 0 mm  [stored 0 ft] | 30.00° | 30.00° |
| DO3, 20 W, 3000 K, 5° | 0 mm  [stored 0 ft] | 45.00° | 45.00° |
| DO3, 20 W, 3000 K, 10° | 0 mm  [stored 0 ft] | 45.00° | 45.00° |
| DO3, 20 W, 3000 K, 15° | 0 mm  [stored 0 ft] | 45.00° | 45.00° |
| DO3, 20 W, 3000 K, 20° | 0 mm  [stored 0 ft] | 45.00° | 45.00° |
| DO3, 20 W, 3000 K, 25° | 0 mm  [stored 0 ft] | 45.00° | 45.00° |
| DO3, 20 W, 3000 K, 30° | 0 mm  [stored 0 ft] | 45.00° | 45.00° |
| DO3, 20 W, 3000 K, 35° | 0 mm  [stored 0 ft] | 45.00° | 45.00° |
| DO3, 20 W, 3000 K, 40° | 0 mm  [stored 0 ft] | 45.00° | 45.00° |
| DO3, 20 W, 3000 K, 45° | 0 mm  [stored 0 ft] | 45.00° | 45.00° |
| DO3, 20 W, 3000 K, 50° | 0 mm  [stored 0 ft] | 45.00° | 45.00° |
| DO3, 20 W, 3000 K, 55° | 0 mm  [stored 0 ft] | 45.00° | 45.00° |
| DO3, 20 W, 3000 K, 60° | 0 mm  [stored 0 ft] | 45.00° | 45.00° |
| DO3, 20 W, 3000 K, 65° | 0 mm  [stored 0 ft] | 45.00° | 45.00° |
| DO3, 20 W, 3000 K, 70° | 0 mm  [stored 0 ft] | 45.00° | 45.00° |
| DO3, 20 W, 3000 K, 75° | 0 mm  [stored 0 ft] | 45.00° | 45.00° |
| DO3, 20 W, 3000 K, 80° | 0 mm  [stored 0 ft] | 45.00° | 45.00° |
| DO3, 20 W, 3000 K, 85° | 0 mm  [stored 0 ft] | 45.00° | 45.00° |
| DO3, 20 W, 3000 K, 95° | 0 mm  [stored 0 ft] | 45.00° | 45.00° |
| DO3, 20 W, 3000 K, 100° | 0 mm  [stored 0 ft] | 45.00° | 45.00° |
| DO3, 20 W, 3000 K, 105° | 0 mm  [stored 0 ft] | 45.00° | 45.00° |
| DO3, 20 W, 3000 K, 110° | 0 mm  [stored 0 ft] | 45.00° | 45.00° |
| DO3, 20 W, 3000 K, 115° | 0 mm  [stored 0 ft] | 45.00° | 45.00° |
| DO3, 20 W, 3000 K, 120° | 0 mm  [stored 0 ft] | 45.00° | 45.00° |
| DO3, 20 W, 3000 K, 125° | 0 mm  [stored 0 ft] | 45.00° | 45.00° |
| DO3, 20 W, 3000 K, 130° | 0 mm  [stored 0 ft] | 45.00° | 45.00° |
| DO3, 20 W, 3000 K, 135° | 0 mm  [stored 0 ft] | 45.00° | 45.00° |
| DO3, 20 W, 3000 K, 140° | 0 mm  [stored 0 ft] | 45.00° | 45.00° |
| DO3, 20 W, 3000 K, 145° | 0 mm  [stored 0 ft] | 45.00° | 45.00° |
| DO3, 20 W, 3000 K, 150° | 0 mm  [stored 0 ft] | 45.00° | 45.00° |
| DO3, 20 W, 3000 K, 155° | 0 mm  [stored 0 ft] | 45.00° | 45.00° |
| DO3, 20 W, 3000 K, 160° | 0 mm  [stored 0 ft] | 45.00° | 45.00° |
| DO3, 20 W, 3000 K, 165° | 0 mm  [stored 0 ft] | 45.00° | 45.00° |
| DO3, 20 W, 3000 K, 170° | 0 mm  [stored 0 ft] | 45.00° | 45.00° |
| DO3, 20 W, 3000 K, 175° | 0 mm  [stored 0 ft] | 45.00° | 45.00° |
| DO3, 20 W, 4000 K, 5° | 0 mm  [stored 0 ft] | 45.00° | 45.00° |
| DO3, 20 W, 4000 K, 10° | 0 mm  [stored 0 ft] | 45.00° | 45.00° |
| DO3, 20 W, 4000 K, 15° | 0 mm  [stored 0 ft] | 45.00° | 45.00° |
| DO3, 20 W, 4000 K, 20° | 0 mm  [stored 0 ft] | 45.00° | 45.00° |
| DO3, 20 W, 4000 K, 25° | 0 mm  [stored 0 ft] | 45.00° | 45.00° |
| DO3, 20 W, 4000 K, 30° | 0 mm  [stored 0 ft] | 45.00° | 45.00° |
| DO3, 20 W, 4000 K, 35° | 0 mm  [stored 0 ft] | 45.00° | 45.00° |
| DO3, 20 W, 4000 K, 40° | 0 mm  [stored 0 ft] | 45.00° | 45.00° |
| DO3, 20 W, 4000 K, 45° | 0 mm  [stored 0 ft] | 45.00° | 45.00° |
| DO3, 20 W, 4000 K, 50° | 0 mm  [stored 0 ft] | 45.00° | 45.00° |
| DO3, 20 W, 4000 K, 55° | 0 mm  [stored 0 ft] | 45.00° | 45.00° |
| DO3, 20 W, 4000 K, 60° | 0 mm  [stored 0 ft] | 45.00° | 45.00° |
| DO3, 20 W, 4000 K, 65° | 0 mm  [stored 0 ft] | 45.00° | 45.00° |
| DO3, 20 W, 4000 K, 70° | 0 mm  [stored 0 ft] | 45.00° | 45.00° |
| DO3, 20 W, 4000 K, 75° | 0 mm  [stored 0 ft] | 45.00° | 45.00° |
| DO3, 20 W, 4000 K, 80° | 0 mm  [stored 0 ft] | 45.00° | 45.00° |
| DO3, 20 W, 4000 K, 85° | 0 mm  [stored 0 ft] | 45.00° | 45.00° |
| DO3, 20 W, 4000 K, 95° | 0 mm  [stored 0 ft] | 45.00° | 45.00° |
| DO3, 20 W, 4000 K, 100° | 0 mm  [stored 0 ft] | 45.00° | 45.00° |
| DO3, 20 W, 4000 K, 105° | 0 mm  [stored 0 ft] | 45.00° | 45.00° |
| DO3, 20 W, 4000 K, 110° | 0 mm  [stored 0 ft] | 45.00° | 45.00° |
| DO3, 20 W, 4000 K, 115° | 0 mm  [stored 0 ft] | 45.00° | 45.00° |
| DO3, 20 W, 4000 K, 120° | 0 mm  [stored 0 ft] | 45.00° | 45.00° |
| DO3, 20 W, 4000 K, 125° | 0 mm  [stored 0 ft] | 45.00° | 45.00° |
| DO3, 20 W, 4000 K, 130° | 0 mm  [stored 0 ft] | 45.00° | 45.00° |
| DO3, 20 W, 4000 K, 135° | 0 mm  [stored 0 ft] | 45.00° | 45.00° |
| DO3, 20 W, 4000 K, 140° | 0 mm  [stored 0 ft] | 45.00° | 45.00° |
| DO3, 20 W, 4000 K, 145° | 0 mm  [stored 0 ft] | 45.00° | 45.00° |
| DO3, 20 W, 4000 K, 150° | 0 mm  [stored 0 ft] | 45.00° | 45.00° |
| DO3, 20 W, 4000 K, 155° | 0 mm  [stored 0 ft] | 45.00° | 45.00° |
| DO3, 20 W, 4000 K, 160° | 0 mm  [stored 0 ft] | 45.00° | 45.00° |
| DO3, 20 W, 4000 K, 165° | 0 mm  [stored 0 ft] | 45.00° | 45.00° |
| DO3, 20 W, 4000 K, 170° | 0 mm  [stored 0 ft] | 45.00° | 45.00° |
| DO3, 20 W, 4000 K, 175° | 0 mm  [stored 0 ft] | 45.00° | 45.00° |
| DO3, 270 W, 3000 K, 5° | 0 mm  [stored 0 ft] | 45.00° | 45.00° |
| DO3, 270 W, 3000 K, 10° | 0 mm  [stored 0 ft] | 45.00° | 45.00° |
| DO3, 270 W, 3000 K, 15° | 0 mm  [stored 0 ft] | 45.00° | 45.00° |
| DO3, 270 W, 3000 K, 20° | 0 mm  [stored 0 ft] | 45.00° | 45.00° |
| DO3, 270 W, 3000 K, 25° | 0 mm  [stored 0 ft] | 45.00° | 45.00° |
| DO3, 270 W, 3000 K, 30° | 0 mm  [stored 0 ft] | 45.00° | 45.00° |
| DO3, 270 W, 3000 K, 35° | 0 mm  [stored 0 ft] | 45.00° | 45.00° |
| DO3, 270 W, 3000 K, 40° | 0 mm  [stored 0 ft] | 45.00° | 45.00° |
| DO3, 270 W, 3000 K, 45° | 0 mm  [stored 0 ft] | 45.00° | 45.00° |
| DO3, 270 W, 3000 K, 50° | 0 mm  [stored 0 ft] | 45.00° | 45.00° |
| DO3, 270 W, 3000 K, 55° | 0 mm  [stored 0 ft] | 45.00° | 45.00° |
| DO3, 270 W, 3000 K, 60° | 0 mm  [stored 0 ft] | 45.00° | 45.00° |
| DO3, 270 W, 3000 K, 65° | 0 mm  [stored 0 ft] | 45.00° | 45.00° |
| DO3, 270 W, 3000 K, 70° | 0 mm  [stored 0 ft] | 45.00° | 45.00° |
| DO3, 270 W, 3000 K, 75° | 0 mm  [stored 0 ft] | 45.00° | 45.00° |
| DO3, 270 W, 3000 K, 80° | 0 mm  [stored 0 ft] | 45.00° | 45.00° |
| DO3, 270 W, 3000 K, 85° | 0 mm  [stored 0 ft] | 45.00° | 45.00° |
| DO3, 270 W, 3000 K, 95° | 0 mm  [stored 0 ft] | 45.00° | 45.00° |
| DO3, 270 W, 3000 K, 100° | 0 mm  [stored 0 ft] | 45.00° | 45.00° |
| DO3, 270 W, 3000 K, 105° | 0 mm  [stored 0 ft] | 45.00° | 45.00° |
| DO3, 270 W, 3000 K, 110° | 0 mm  [stored 0 ft] | 45.00° | 45.00° |
| DO3, 270 W, 3000 K, 115° | 0 mm  [stored 0 ft] | 45.00° | 45.00° |
| DO3, 270 W, 3000 K, 120° | 0 mm  [stored 0 ft] | 45.00° | 45.00° |
| DO3, 270 W, 3000 K, 125° | 0 mm  [stored 0 ft] | 45.00° | 45.00° |
| DO3, 270 W, 3000 K, 130° | 0 mm  [stored 0 ft] | 45.00° | 45.00° |
| DO3, 270 W, 3000 K, 135° | 0 mm  [stored 0 ft] | 45.00° | 45.00° |
| DO3, 270 W, 3000 K, 140° | 0 mm  [stored 0 ft] | 45.00° | 45.00° |
| DO3, 270 W, 3000 K, 145° | 0 mm  [stored 0 ft] | 45.00° | 45.00° |
| DO3, 270 W, 3000 K, 150° | 0 mm  [stored 0 ft] | 45.00° | 45.00° |
| DO3, 270 W, 3000 K, 155° | 0 mm  [stored 0 ft] | 45.00° | 45.00° |
| DO3, 270 W, 3000 K, 160° | 0 mm  [stored 0 ft] | 45.00° | 45.00° |
| DO3, 270 W, 3000 K, 165° | 0 mm  [stored 0 ft] | 45.00° | 45.00° |
| DO3, 270 W, 3000 K, 170° | 0 mm  [stored 0 ft] | 45.00° | 45.00° |
| DO3, 270 W, 3000 K, 175° | 0 mm  [stored 0 ft] | 45.00° | 45.00° |
| DO3, 270 W, 4000 K, 5° | 0 mm  [stored 0 ft] | 45.00° | 45.00° |
| DO3, 270 W, 4000 K, 10° | 0 mm  [stored 0 ft] | 45.00° | 45.00° |
| DO3, 270 W, 4000 K, 15° | 0 mm  [stored 0 ft] | 45.00° | 45.00° |
| DO3, 270 W, 4000 K, 20° | 0 mm  [stored 0 ft] | 45.00° | 45.00° |
| DO3, 270 W, 4000 K, 25° | 0 mm  [stored 0 ft] | 45.00° | 45.00° |
| DO3, 270 W, 4000 K, 30° | 0 mm  [stored 0 ft] | 45.00° | 45.00° |
| DO3, 270 W, 4000 K, 35° | 0 mm  [stored 0 ft] | 45.00° | 45.00° |
| DO3, 270 W, 4000 K, 40° | 0 mm  [stored 0 ft] | 45.00° | 45.00° |
| DO3, 270 W, 4000 K, 45° | 0 mm  [stored 0 ft] | 45.00° | 45.00° |
| DO3, 270 W, 4000 K, 50° | 0 mm  [stored 0 ft] | 45.00° | 45.00° |
| DO3, 270 W, 4000 K, 55° | 0 mm  [stored 0 ft] | 45.00° | 45.00° |
| DO3, 270 W, 4000 K, 60° | 0 mm  [stored 0 ft] | 45.00° | 45.00° |
| DO3, 270 W, 4000 K, 65° | 0 mm  [stored 0 ft] | 45.00° | 45.00° |
| DO3, 270 W, 4000 K, 70° | 0 mm  [stored 0 ft] | 45.00° | 45.00° |
| DO3, 270 W, 4000 K, 75° | 0 mm  [stored 0 ft] | 45.00° | 45.00° |
| DO3, 270 W, 4000 K, 80° | 0 mm  [stored 0 ft] | 45.00° | 45.00° |
| DO3, 270 W, 4000 K, 85° | 0 mm  [stored 0 ft] | 45.00° | 45.00° |
| DO3, 270 W, 4000 K, 95° | 0 mm  [stored 0 ft] | 45.00° | 45.00° |
| DO3, 270 W, 4000 K, 100° | 0 mm  [stored 0 ft] | 45.00° | 45.00° |
| DO3, 270 W, 4000 K, 105° | 0 mm  [stored 0 ft] | 45.00° | 45.00° |
| DO3, 270 W, 4000 K, 110° | 0 mm  [stored 0 ft] | 45.00° | 45.00° |
| DO3, 270 W, 4000 K, 115° | 0 mm  [stored 0 ft] | 45.00° | 45.00° |
| DO3, 270 W, 4000 K, 120° | 0 mm  [stored 0 ft] | 45.00° | 45.00° |
| DO3, 270 W, 4000 K, 125° | 0 mm  [stored 0 ft] | 45.00° | 45.00° |
| DO3, 270 W, 4000 K, 130° | 0 mm  [stored 0 ft] | 45.00° | 45.00° |
| DO3, 270 W, 4000 K, 135° | 0 mm  [stored 0 ft] | 45.00° | 45.00° |
| DO3, 270 W, 4000 K, 140° | 0 mm  [stored 0 ft] | 45.00° | 45.00° |
| DO3, 270 W, 4000 K, 145° | 0 mm  [stored 0 ft] | 45.00° | 45.00° |
| DO3, 270 W, 4000 K, 150° | 0 mm  [stored 0 ft] | 45.00° | 45.00° |
| DO3, 270 W, 4000 K, 155° | 0 mm  [stored 0 ft] | 45.00° | 45.00° |
| DO3, 270 W, 4000 K, 160° | 0 mm  [stored 0 ft] | 45.00° | 45.00° |
| DO3, 270 W, 4000 K, 165° | 0 mm  [stored 0 ft] | 45.00° | 45.00° |
| DO3, 270 W, 4000 K, 170° | 0 mm  [stored 0 ft] | 45.00° | 45.00° |
| DO3, 270 W, 4000 K, 175° | 0 mm  [stored 0 ft] | 45.00° | 45.00° |

note: [stored X ft] marks values corroborated as IEEE doubles in the binary element streams (Revit-internal decimal feet)

## geometry (parser evidence)
native form markers: Sweep x2
no freeform markers — native parametric forms only
